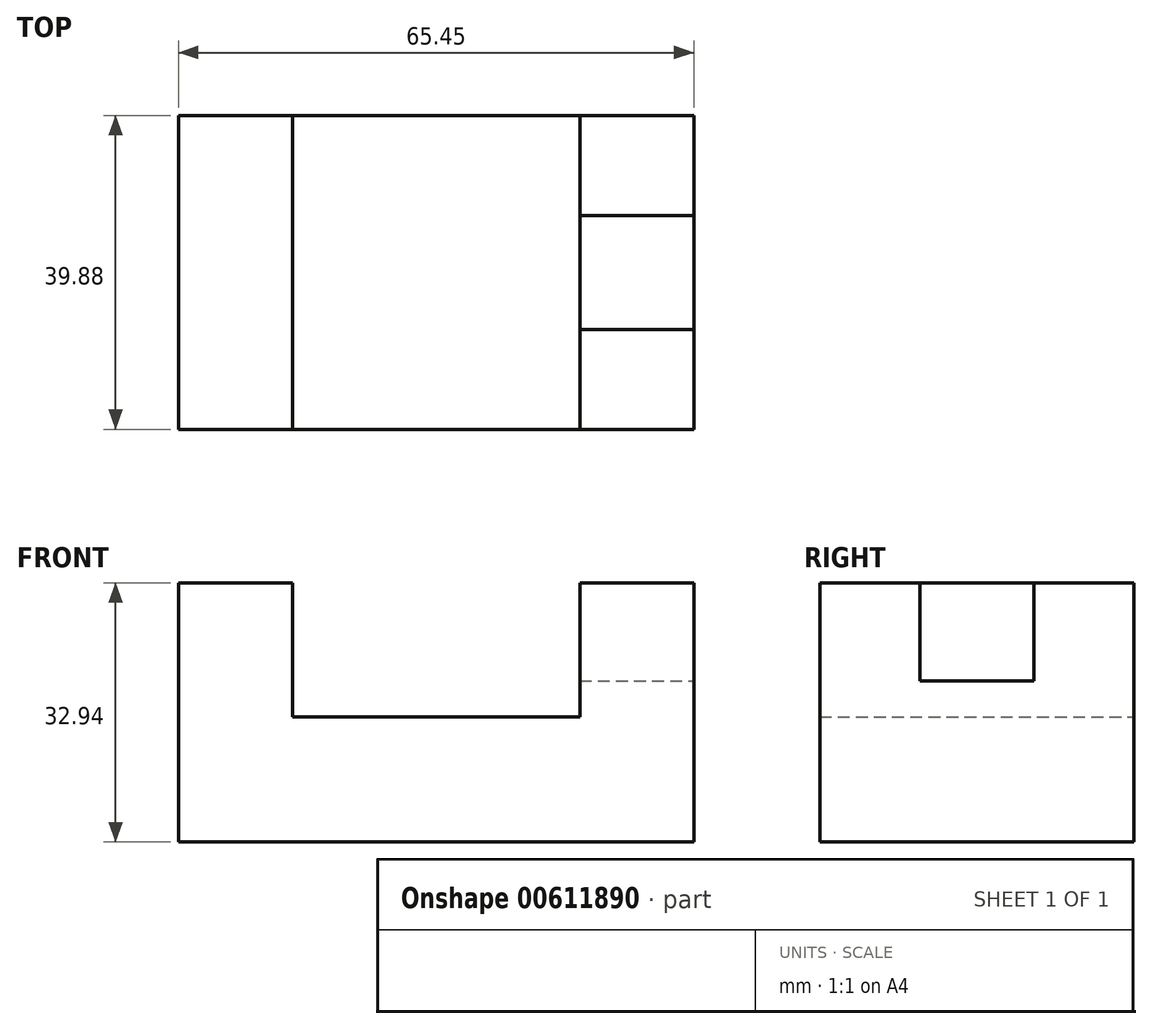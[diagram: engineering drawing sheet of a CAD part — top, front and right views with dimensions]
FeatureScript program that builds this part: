
annotation { "Feature Type Name" : "Feature", "Feature Type Description" : "" }
export const myFeature = defineFeature(function(context is Context, id is Id, definition is map)
    precondition{}
    {
        {
            var Q0;
            Q0=qCreatedBy(makeId("Front.planeOp"),FACE);
            var sketch = newSketch(context, id + "F0", { "sketchPlane" : qUnion([Q0])});
            skLineSegment(sketch, "E0.bottom", {"start": v(0, 0) * mm, "end": v(65.45, 0) * mm});
            skLineSegment(sketch, "E0.top", {"start": v(0, 32.94) * mm, "end": v(14.48, 32.94) * mm});
            skLineSegment(sketch, "E0.left", {"start": v(0, 0) * mm, "end": v(0, 32.94) * mm});
            skLineSegment(sketch, "E0.right", {"start": v(65.45, 0) * mm, "end": v(65.45, 32.94) * mm});
            skLineSegment(sketch, "E1.bottom", {"start": v(50.97, 15.9) * mm, "end": v(14.48, 15.9) * mm});
            skLineSegment(sketch, "E1.left", {"start": v(50.97, 15.9) * mm, "end": v(50.97, 32.94) * mm});
            skLineSegment(sketch, "E1.right", {"start": v(14.48, 15.9) * mm, "end": v(14.48, 32.94) * mm});
            skPoint(sketch, "E1.middle", {"position": v(32.72, 32.94) * mm});
            skPoint(sketch, "E2.orphan", {"position": v(14.48, 49.97) * mm});
            skLineSegment(sketch, "E3.trimOffspring", {"start": v(50.97, 32.94) * mm, "end": v(65.45, 32.94) * mm});
            skPoint(sketch, "E4.orphan", {"position": v(50.97, 49.97) * mm});
            skSolve(sketch);
        }
        {
            var Q0;
            Q0 = qSketchRegion(id + "F0", true);
            extrude(context, id + "F1", {"entities" : qUnion([Q0]), "depth" : 39.88 * mm, "offsetDistance" : 25.4 * mm});
        }
        {
            var Q0;
            Q0=makeQuery(id+"F1.opExtrude","SWEPT_FACE",FACE,{"disambiguationData":[OSD([sQuery(id+"F0.wireOp",EDGE,"E3.trimOffspring")])]});
            var sketch = newSketch(context, id + "F2", { "sketchPlane" : qUnion([Q0])});
            skLineSegment(sketch, "E5", {"start": v(50.97, -27.18) * mm, "end": v(65.45, -27.18) * mm});
            skLineSegment(sketch, "E6", {"start": v(65.45, -27.18) * mm, "end": v(65.45, -12.7) * mm});
            skLineSegment(sketch, "E7", {"start": v(65.45, -12.7) * mm, "end": v(50.97, -12.7) * mm});
            skLineSegment(sketch, "E8", {"start": v(50.97, -12.7) * mm, "end": v(50.97, -27.18) * mm});
            skLineSegment(sketch, "E9", {"start": v(50.97, -19.94) * mm, "end": v(65.45, -19.94) * mm, "construction": true});
            skLineSegment(sketch, "E10", {"start": v(58.2, -12.7) * mm, "end": v(58.2, -27.18) * mm, "construction": true});
            skCircle(sketch, "E11", {"center": v(58.2, -19.94) * mm, "radius": 3.76 * mm, "construction": true});
            skSolve(sketch);
        }
        {
            var Q0;
            Q0=makeQuery(id+"F2.imprint","IMPRINT",FACE,{"disambiguationData":[TD([[makeQuery(id+"F2.imprint","IMPRINT",EDGE,{"derivedFrom":sQuery(id+"F2.wireOp",EDGE,"E5")}),1.0]])]});
            var Q1;
            Q1 = qConstructionFilter(qBodyType(qCreatedBy(id + "F2" ,EDGE), BodyType.WIRE), ConstructionObject.NO);
            extrude(context, id + "F3", {"entities" : qUnion([Q0]), "operationType" : NewBodyOperationType.REMOVE, "surfaceEntities" : qUnion([Q1]), "oppositeDirection" : true, "depth" : 12.45 * mm, "offsetDistance" : 25.4 * mm});
        }
    });
